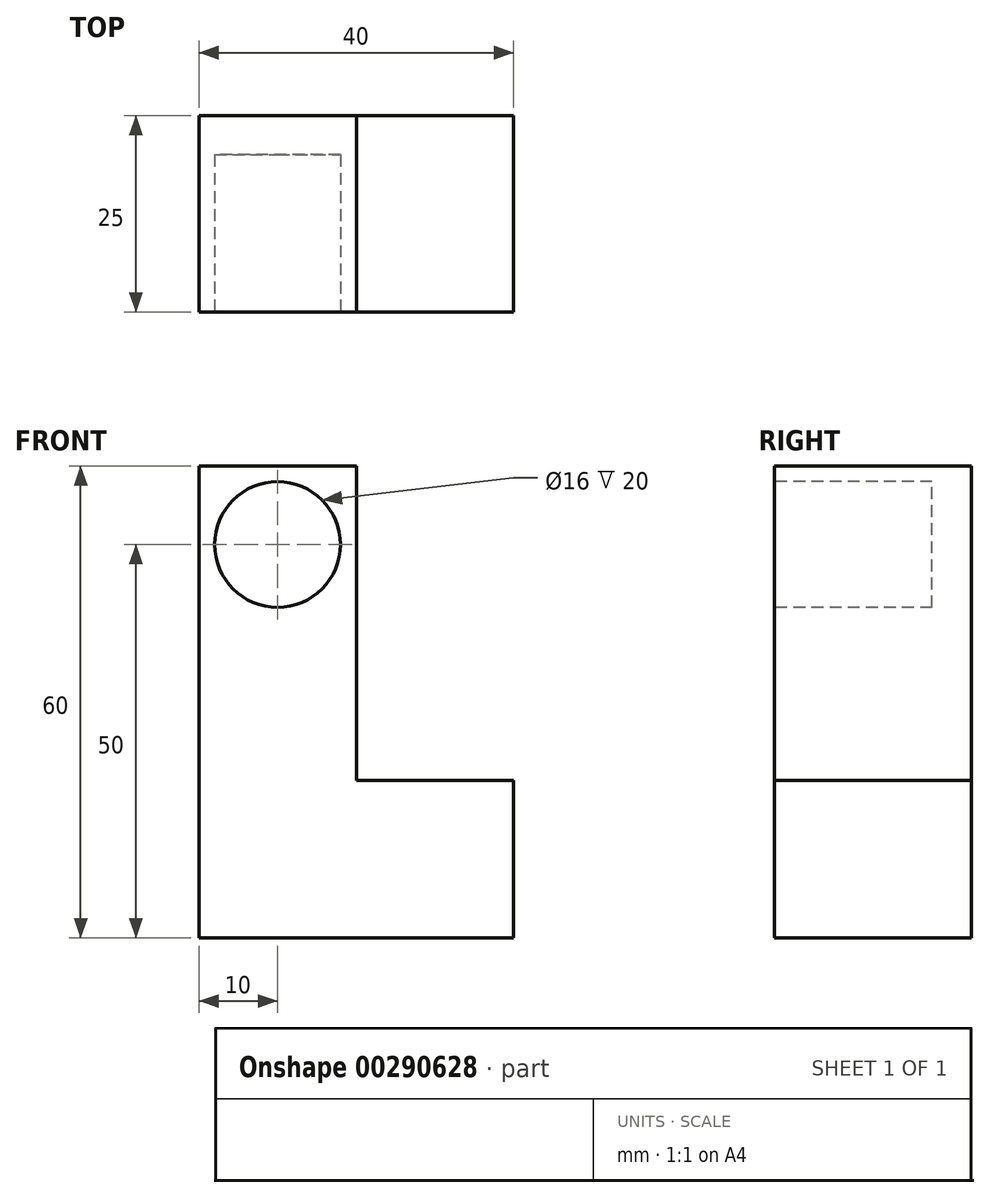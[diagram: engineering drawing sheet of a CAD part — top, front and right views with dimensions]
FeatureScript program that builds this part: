
annotation { "Feature Type Name" : "Feature", "Feature Type Description" : "" }
export const myFeature = defineFeature(function(context is Context, id is Id, definition is map)
    precondition{}
    {
        {
            var Q0;
            Q0=qCreatedBy(makeId("Top.planeOp"),FACE);
            var sketch = newSketch(context, id + "F0", { "sketchPlane" : qUnion([Q0])});
            skLineSegment(sketch, "E0.bottom", {"start": v(-20, 12.5) * mm, "end": v(20, 12.5) * mm});
            skLineSegment(sketch, "E0.top", {"start": v(-20, -12.5) * mm, "end": v(20, -12.5) * mm});
            skLineSegment(sketch, "E0.left", {"start": v(-20, 12.5) * mm, "end": v(-20, -12.5) * mm});
            skLineSegment(sketch, "E0.right", {"start": v(20, 12.5) * mm, "end": v(20, -12.5) * mm});
            skLineSegment(sketch, "E1", {"start": v(0, 12.5) * mm, "end": v(0, -12.5) * mm, "construction": true});
            skLineSegment(sketch, "E2", {"start": v(-20, 0) * mm, "end": v(20, 0) * mm, "construction": true});
            skPoint(sketch, "E2.startSnap0", {"position": v(-20, 0) * mm});
            skLineSegment(sketch, "E3", {"start": v(0, 12.5) * mm, "end": v(0, -12.5) * mm});
            skSolve(sketch);
        }
        {
            var Q0;
            {var subQ0=sQuery(id+"F0.wireOp",EDGE,"E0.left");Q0=makeQuery(id+"F0.imprint","IMPRINT",FACE,{"disambiguationData":[TD([[makeQuery(id+"F0.imprint","IMPRINT",EDGE,{"derivedFrom":subQ0}),1.0]])]});}
            extrude(context, id + "F1", {"entities" : qUnion([Q0]), "depth" : 60 * mm});
        }
        {
            var Q0;
            {var subQ0=sQuery(id+"F0.wireOp",EDGE,"E0.right");Q0=makeQuery(id+"F0.imprint","IMPRINT",FACE,{"disambiguationData":[TD([[makeQuery(id+"F0.imprint","IMPRINT",EDGE,{"derivedFrom":subQ0}),-1.0]])]});}
            extrude(context, id + "F2", {"entities" : qUnion([Q0]), "operationType" : NewBodyOperationType.ADD, "depth" : 20 * mm});
        }
        {
            var Q0;
            {var subQ0=sQuery(id+"F0.wireOp",EDGE,"E0.top");Q0=makeQuery(id+"F2.boolean.opBoolean","MERGE",FACE,{"derivedFrom":[makeQuery(id+"F1.opExtrude","SWEPT_FACE",FACE,{"disambiguationData":[OSD([subQ0])]}),makeQuery(id+"F2.opExtrude","SWEPT_FACE",FACE,{"disambiguationData":[OSD([subQ0])]})]});}
            var sketch = newSketch(context, id + "F3", { "sketchPlane" : qUnion([Q0])});
            skLineSegment(sketch, "E4", {"start": v(-10, 60) * mm, "end": v(-10, 0) * mm, "construction": true});
            skPoint(sketch, "E5.trimOffspring.end.orphan", {"position": v(-20, 30) * mm});
            skPoint(sketch, "E6.center.orphan", {"position": v(-10, 25) * mm});
            skPoint(sketch, "E7.start.orphan", {"position": v(0, 20) * mm});
            skLineSegment(sketch, "E8", {"start": v(-20, 50) * mm, "end": v(0, 50) * mm, "construction": true});
            skCircle(sketch, "E9", {"center": v(-10, 50) * mm, "radius": 8 * mm});
            skSolve(sketch);
        }
        {
            var Q0;
            Q0=makeQuery(id+"F3.imprint","IMPRINT",FACE,{"disambiguationData":[TD([[makeQuery(id+"F3.imprint","IMPRINT",EDGE,{"derivedFrom":sQuery(id+"F3.wireOp",EDGE,"E9")}),1.0]])]});
            extrude(context, id + "F4", {"entities" : qUnion([Q0]), "operationType" : NewBodyOperationType.REMOVE, "oppositeDirection" : true, "depth" : 20 * mm});
        }
    });
